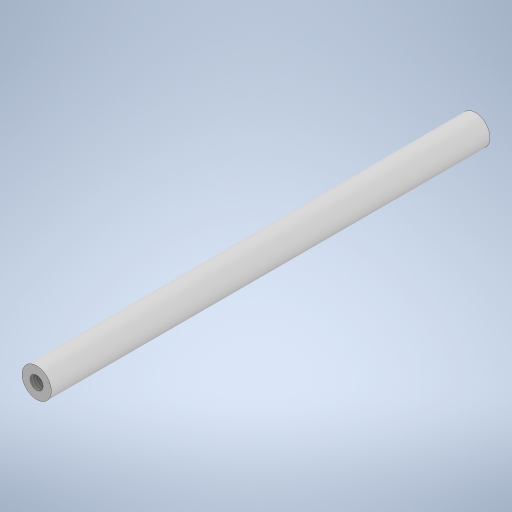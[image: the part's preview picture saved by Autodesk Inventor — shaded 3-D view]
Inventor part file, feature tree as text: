
AUTODESK INVENTOR PART (.ipt)
format: ipt  version: 2023 (Build 270158000, 158)  size: 263,680 bytes
history: native  units: mm
features: extrude x3, sketch x3, thread x2
ambient origin geometry x8: Origin, YZ Plane, XZ Plane, XY Plane, X Axis, Y Axis, Z Axis, Center Point
bodies: Solid1 (feature_tree)
feature tree (8):
  extrude  "Extrusion1"  Depth=75.0mm TaperAngle=0.0deg
  extrude  "Extrusion2"  Depth=20.0mm TaperAngle=0.0deg
  extrude  "Extrusion3"  Depth=20.0mm TaperAngle=0.0deg
  thread  "Thread1"  [1 undecoded]
  thread  "Thread2"  [1 undecoded]
  sketch  "Sketch1"  dims[d0=5.0mm d1=75.0mm d2=0.0mm]
  sketch  "Sketch2"  dims[d3=2.2mm d4=20.0mm d5=0.0mm]
  sketch  "Sketch3"  dims[d6=20.0mm d7=0.0mm d8=16.0mm d9=0.0mm d10=16.0mm d11=0.0mm]
note: 2 required parameter values undecoded (feature->parameter linkage not recoverable at this tier; creation-order binding heuristic only, values carry confidence <= 0.55)
